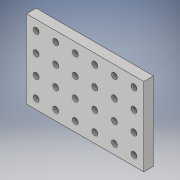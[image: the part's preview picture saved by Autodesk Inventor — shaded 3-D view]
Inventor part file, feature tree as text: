
AUTODESK INVENTOR PART (.ipt)
format: ipt  version: 2018 (Build 220112000, 112)  size: 131,072 bytes
history: native  units: in
note: dims shown in document units (in); Inventor stores cm internally (conversion verified against a paired STEP export)
features: extrude x2, sketch x2, pattern_linear x1
ambient origin geometry x8: Origin, YZ Plane, XZ Plane, XY Plane, X Axis, Y Axis, Z Axis, Center Point
bodies: Solid1 (feature_tree)
feature tree (5):
  extrude  "Extrusion1"  Depth=4.0in
  extrude  "Extrusion2"  Depth=0.5in
  pattern_linear  "Rectangular Pattern1"  Spacing1=0.5in  [1 undecoded]
  sketch  "Sketch1"  dims[d0=6.0in d1=4.0in]
  sketch  "Sketch2"  dims[d2=0.5in d3=0.0in d4=0.3in d5=0.5in d6=0.5in d7=0.5in d8=0.0in d9=1.5748in d11=1.0in d12=2.3622in d14=1.0in]
note: 1 required parameter value undecoded (feature->parameter linkage not recoverable at this tier; creation-order binding heuristic only, values carry confidence <= 0.55)
